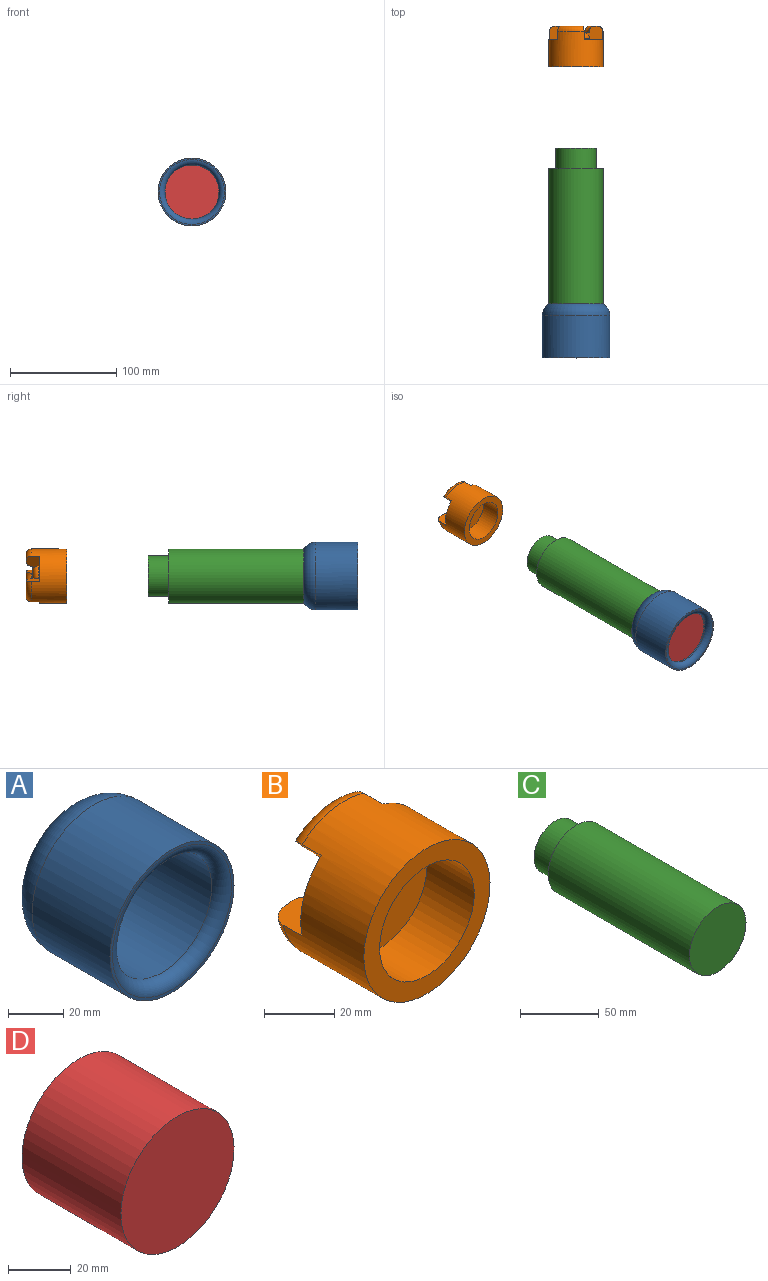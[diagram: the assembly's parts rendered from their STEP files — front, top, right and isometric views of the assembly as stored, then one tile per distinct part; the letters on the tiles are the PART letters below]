
ASSEMBLY  parts=4 mates=3
PART A: 5 faces, bbox 73.8x52.5x73.8 mm
  f0: cylinder r=25.4mm len=50.8mm, axis (0,1,0), area 7296.6mm2, adj f3,f4
  f1: cylinder r=31.75mm len=63.5mm, axis (0,1,0), area 7940mm2, adj f2,f3
  f2: plane 63.5x63.5mm, normal (0,-1,0), area 248.3mm2, adj f1,f4
  f3: torus R=19.05mm, axis (0,1,0), area 2469.5mm2, adj f0,f1
  f4: torus R=30.48mm, axis (0,-1,0), area 1366mm2, adj f0,f2
PART B: 32 faces, bbox 54.3x38.1x53.7 mm
  f0: cylinder r=12.7mm len=12.12mm, axis (0,-1,0), area 16.9mm2, adj f1,f14,f19,f22
  f1: plane 24.24x16.8mm, normal (0,1,0), area 253.4mm2, adj f0,f5,f14,f19
  f2: cylinder r=12.7mm len=12.39mm, axis (0,-1,0), area 16.9mm2, adj f3,f10,f15,f23
  f3: plane 24.79x16.05mm, normal (0,1,0), area 253.4mm2, adj f2,f5,f10,f15
  f4: cylinder r=12.7mm len=9.35mm, axis (0,-1,0), area 16.9mm2, adj f7,f11,f18,f21
  f5: cylinder r=25.4mm len=50.8mm, axis (0,1,0), area 4661.7mm2, adj f1,f3,f6,f7,f10,f11,f14,f15
  f6: plane 50.8x50.8mm, normal (0,-1,0), area 886.7mm2, adj f5,f30
  f7: plane 21.47x20.99mm, normal (0,1,0), area 253.4mm2, adj f4,f5,f11,f18
  f8: plane 25.09x24.82mm, normal (0,1,0), area 344.6mm2, adj f9,f10,f11,f13,f14,f15,f17,f18
  f9: cylinder r=12.7mm len=12.12mm, axis (0,-1,0), area 16.9mm2, adj f8,f10,f11,f26
  f10: plane 13.09x12.7mm, normal (-0.74,0,-0.68), area 155.8mm2, adj f2,f3,f5,f8,f9,f12,f23,f26
  f11: plane 17.35x12.7mm, normal (-0.22,0,0.98), area 155.8mm2, adj f4,f5,f7,f8,f9,f12,f21,f26
  f12: plane 19.39x8.29mm, normal (0,1,0), area 50.7mm2, adj f10,f11,f26,f27
  f13: cylinder r=12.7mm len=9.35mm, axis (0,-1,0), area 16.9mm2, adj f8,f14,f15,f24
  f14: plane 17.35x12.7mm, normal (-0.22,0,0.98), area 155.8mm2, adj f0,f1,f5,f8,f13,f16,f22,f24
  f15: plane 16.97x12.7mm, normal (0.95,0,-0.3), area 155.8mm2, adj f2,f3,f5,f8,f13,f16,f23,f24
  f16: plane 15.51x14.51mm, normal (0,1,0), area 50.7mm2, adj f14,f15,f24,f25
  f17: cylinder r=12.7mm len=12.39mm, axis (0,-1,0), area 16.9mm2, adj f8,f18,f19,f28
  f18: plane 16.97x12.7mm, normal (0.95,0,-0.3), area 155.8mm2, adj f4,f5,f7,f8,f17,f20,f21,f28
  f19: plane 13.09x12.7mm, normal (-0.74,0,-0.68), area 155.8mm2, adj f0,f1,f5,f8,f17,f20,f22,f28
  f20: plane 19.83x7.23mm, normal (0,1,0), area 50.7mm2, adj f18,f19,f28,f29
  f21: torus R=7.62mm, axis (0,1,0), area 90.7mm2, adj f4,f8,f11,f18
  f22: torus R=7.62mm, axis (0,1,0), area 90.7mm2, adj f0,f8,f14,f19
  f23: torus R=7.62mm, axis (0,1,0), area 90.7mm2, adj f2,f8,f10,f15
  f24: torus R=17.78mm, axis (0,1,0), area 121.5mm2, adj f13,f14,f15,f16
  f25: torus R=20.32mm, axis (0,1,0), area 196.8mm2, adj f5,f14,f15,f16
  f26: torus R=17.78mm, axis (0,1,0), area 121.5mm2, adj f9,f10,f11,f12
  f27: torus R=20.32mm, axis (0,1,0), area 196.8mm2, adj f5,f10,f11,f12
  f28: torus R=17.78mm, axis (0,1,0), area 121.5mm2, adj f17,f18,f19,f20
  f29: torus R=20.32mm, axis (0,1,0), area 196.8mm2, adj f5,f18,f19,f20
  f30: cylinder r=19.05mm len=38.1mm, axis (0,-1,0), area 2280.2mm2, adj f6,f31
  f31: plane 38.1x38.1mm, normal (0,-1,0), area 1140.1mm2, adj f30
PART C: 12 faces, bbox 50.8x146.1x50.8 mm
  f0: cylinder r=12.7mm len=25.4mm, axis (0,-1,0), area 506.7mm2, adj f5,f6
  f1: cylinder r=25.4mm len=127mm, axis (0,1,0), area 20268.3mm2, adj f2,f3
  f2: plane 50.8x50.8mm, normal (0,-1,0), area 2026.8mm2, adj f1
  f3: plane 50.8x50.8mm, normal (0,1,0), area 886.7mm2, adj f1,f4
  f4: cylinder r=19.05mm len=38.1mm, axis (0,-1,0), area 2280.2mm2, adj f3,f5
  f5: plane 38.1x38.1mm, normal (0,1,0), area 633.4mm2, adj f0,f4
  f6: plane 25.4x25.4mm, normal (0,1,0), area 442.2mm2, adj f0,f7,f8,f9,f10
  f7: plane 12.7x6.35mm, normal (0,0,-1), area 80.6mm2, adj f6,f8,f10,f11
  f8: plane 6.35x5.08mm, normal (-1,0,0), area 32.3mm2, adj f6,f7,f9,f11
  f9: plane 12.7x6.35mm, normal (0,0,1), area 80.6mm2, adj f6,f8,f10,f11
  f10: plane 6.35x5.08mm, normal (1,0,0), area 32.3mm2, adj f6,f7,f9,f11
  f11: plane 12.7x5.08mm, normal (0,1,0), area 64.5mm2, adj f7,f8,f9,f10
PART D: 3 faces, bbox 50.8x44.5x50.8 mm
  f0: cylinder r=25.4mm len=50.8mm, axis (0,1,0), area 7093.9mm2, adj f1,f2
  f1: plane 50.8x50.8mm, normal (0,-1,0), area 2026.8mm2, adj f0
  f2: plane 50.8x50.8mm, normal (0,1,0), area 2026.8mm2, adj f0
PLACE A t=(-4.67,-272.39,3.92)mm
PLACE B t=(-4.67,-151.13,3.92)mm
PLACE C t=(-4.67,-272.39,3.92)mm
PLACE D t=(-4.67,-272.39,3.92)mm
MATE fastened C.f1 <-> D.f0  axis (0,-1,0) through (-4.67,-399.39,3.92)mm
MATE slider C.f1 <-> B.f5  axis (0,1,0) through (-4.67,-272.39,3.92)mm
MATE fastened A.f0 <-> D.f0  axis (0,-1,0) through (-4.67,-399.39,3.92)mm
